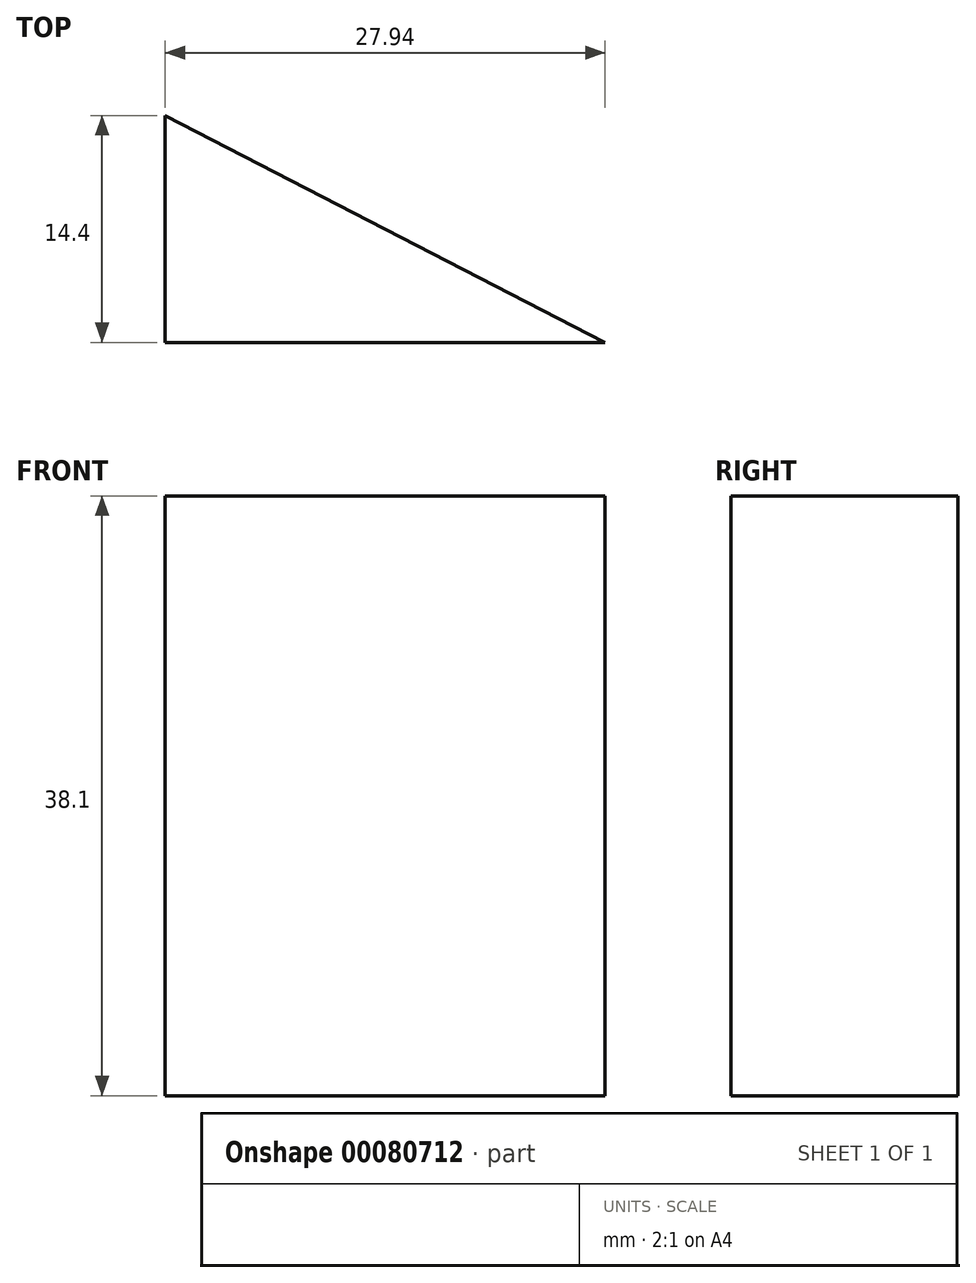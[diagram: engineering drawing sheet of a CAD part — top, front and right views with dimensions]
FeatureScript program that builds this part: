
annotation { "Feature Type Name" : "Feature", "Feature Type Description" : "" }
export const myFeature = defineFeature(function(context is Context, id is Id, definition is map)
    precondition{}
    {
        {
            var Q0;
            Q0=qCreatedBy(makeId("Top.planeOp"),FACE);
            var sketch = newSketch(context, id + "F0", { "sketchPlane" : qUnion([Q0])});
            skLineSegment(sketch, "E0.bottom", {"start": v(-19.26, 19.02) * mm, "end": v(8.68, 19.02) * mm});
            skLineSegment(sketch, "E0.top", {"start": v(-19.26, -6.38) * mm, "end": v(8.68, -6.38) * mm});
            skLineSegment(sketch, "E0.left", {"start": v(-19.26, 19.02) * mm, "end": v(-19.26, -6.38) * mm});
            skLineSegment(sketch, "E0.right", {"start": v(8.68, 19.02) * mm, "end": v(8.68, -6.38) * mm});
            skLineSegment(sketch, "E1", {"start": v(-19.26, 8.02) * mm, "end": v(8.68, -6.38) * mm});
            skSolve(sketch);
        }
        {
            var Q0;
            {var subQ0=sQuery(id+"F0.wireOp",EDGE,"E0.top");Q0=makeQuery(id+"F0.imprint","IMPRINT",FACE,{"disambiguationData":[TD([[makeQuery(id+"F0.imprint","IMPRINT",EDGE,{"derivedFrom":subQ0}),1.0]])]});}
            extrude(context, id + "F1", {"entities" : qUnion([Q0]), "endBound" : BoundingType.SYMMETRIC, "depth" : 38.1 * mm});
        }
    });
